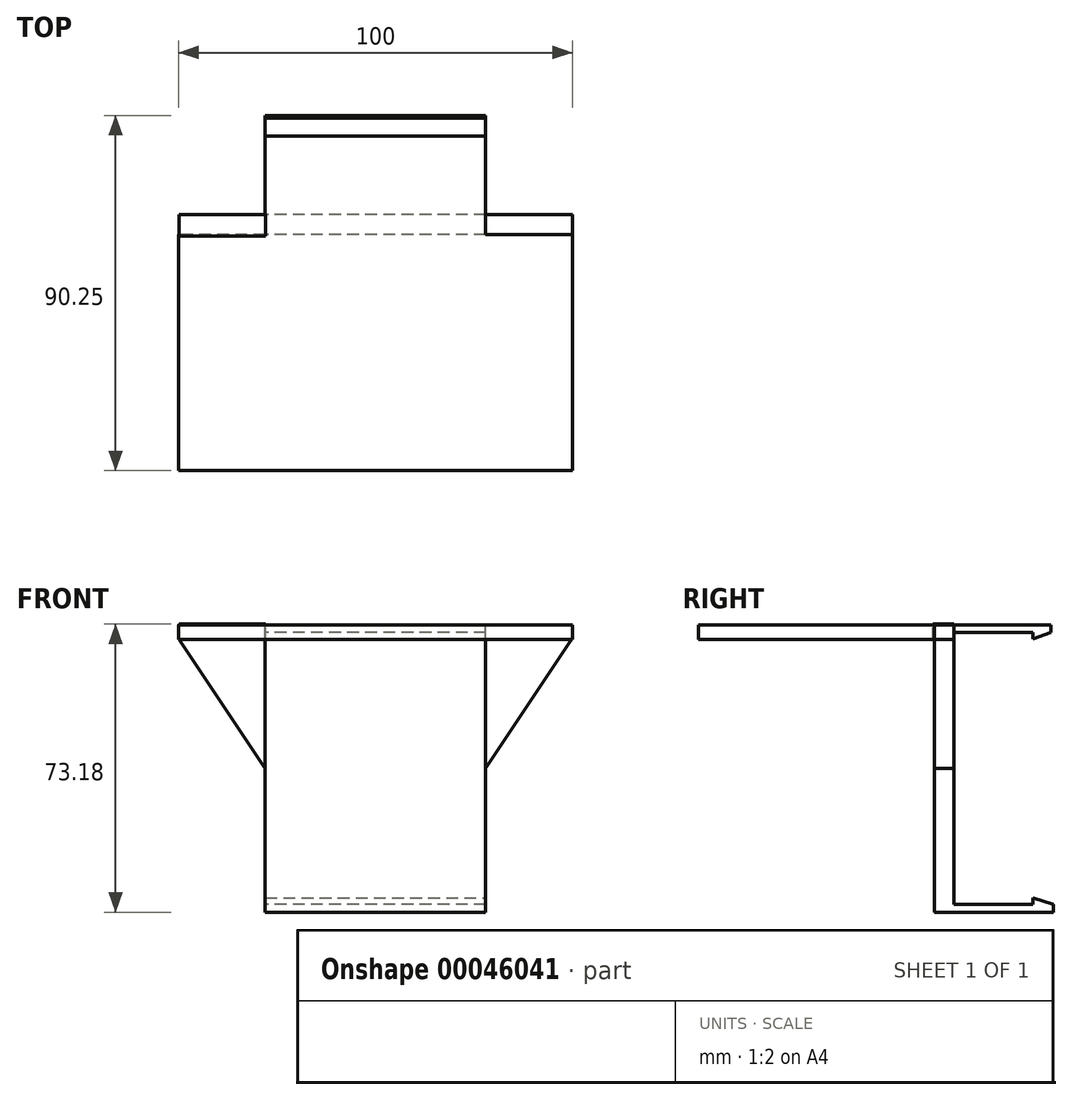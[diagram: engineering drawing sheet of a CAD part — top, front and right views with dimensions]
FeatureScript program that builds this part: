
annotation { "Feature Type Name" : "Feature", "Feature Type Description" : "" }
export const myFeature = defineFeature(function(context is Context, id is Id, definition is map)
    precondition{}
    {
        {
            var Q0;
            Q0=qCreatedBy(makeId("Front.planeOp"),FACE);
            var sketch = newSketch(context, id + "F0", { "sketchPlane" : qUnion([Q0])});
            skLineSegment(sketch, "E0.rect.bottom", {"start": v(28, -34.5) * mm, "end": v(-28, -34.5) * mm});
            skLineSegment(sketch, "E0.rect.top", {"start": v(28, 34.5) * mm, "end": v(-28, 34.5) * mm});
            skLineSegment(sketch, "E0.rect.left", {"start": v(28, -34.5) * mm, "end": v(28, 34.5) * mm});
            skLineSegment(sketch, "E0.rect.right", {"start": v(-28, -34.5) * mm, "end": v(-28, 34.5) * mm});
            skPoint(sketch, "E0.rect.middle", {"position": v(0, 0) * mm});
            skSolve(sketch);
        }
        {
            var Q0;
            Q0=makeQuery(id+"F0.imprint","IMPRINT",FACE,{"disambiguationData":[TD([[makeQuery(id+"F0.imprint","IMPRINT",EDGE,{"derivedFrom":sQuery(id+"F0.wireOp",EDGE,"E0.rect.bottom")}),-1.0]])]});
            extrude(context, id + "F1", {"entities" : qUnion([Q0]), "depth" : 5 * mm});
        }
        {
            var Q0;
            Q0=makeQuery(id+"F1.opExtrude","SWEPT_FACE",FACE,{"disambiguationData":[OSD([sQuery(id+"F0.wireOp",EDGE,"E0.rect.top")])]});
            var sketch = newSketch(context, id + "F2", { "sketchPlane" : qUnion([Q0])});
            skPoint(sketch, "E1.oppositeSnap0", {"position": v(28, -2.5) * mm});
            skLineSegment(sketch, "E1.bottom", {"start": v(-28, -5) * mm, "end": v(28, -5) * mm});
            skLineSegment(sketch, "E1.top", {"start": v(-28, 20) * mm, "end": v(28, 20) * mm});
            skLineSegment(sketch, "E1.left", {"start": v(-28, -5) * mm, "end": v(-28, 20) * mm});
            skLineSegment(sketch, "E1.right", {"start": v(28, -5) * mm, "end": v(28, 20) * mm});
            skSolve(sketch);
        }
        {
            var Q0;
            {var subQ2=sQuery(id+"F2.wireOp",EDGE,"E1.top");Q0=makeQuery(id+"F2.imprint","IMPRINT",FACE,{"disambiguationData":[TD([[makeQuery(id+"F2.imprint","IMPRINT",EDGE,{"derivedFrom":subQ2}),-1.0]])]});}
            var Q1;
            {var subQ2=sQuery(id+"F2.wireOp",EDGE,"E1.bottom");Q1=makeQuery(id+"F2.imprint","IMPRINT",FACE,{"disambiguationData":[TD([[makeQuery(id+"F2.imprint","IMPRINT",EDGE,{"derivedFrom":subQ2}),-1.0]])]});}
            extrude(context, id + "F3", {"entities" : qUnion([Q0, Q1]), "operationType" : NewBodyOperationType.ADD, "depth" : 2 * mm});
        }
        {
            var Q0;
            Q0=makeQuery(id+"F3.boolean.opBoolean","MERGE",FACE,{"derivedFrom":[makeQuery(id+"F1.opExtrude","SWEPT_FACE",FACE,{"disambiguationData":[OSD([sQuery(id+"F0.wireOp",EDGE,"E0.rect.right")])]}),makeQuery(id+"F3.opExtrude","SWEPT_FACE",FACE,{"disambiguationData":[OSD([sQuery(id+"F2.wireOp",EDGE,"E1.left")])]})]});
            var sketch = newSketch(context, id + "F4", { "sketchPlane" : qUnion([Q0])});
            skLineSegment(sketch, "E2.bottom", {"start": v(-20, 34.5) * mm, "end": v(-24.6, 34.5) * mm});
            skLineSegment(sketch, "E2.top", {"start": v(-20, 36.44) * mm, "end": v(-24.6, 36.44) * mm});
            skLineSegment(sketch, "E2.left", {"start": v(-20, 34.5) * mm, "end": v(-20, 36.44) * mm});
            skLineSegment(sketch, "E2.right", {"start": v(-24.6, 34.5) * mm, "end": v(-24.6, 36.44) * mm});
            skLineSegment(sketch, "E3", {"start": v(-24.6, 34.5) * mm, "end": v(-20, 32.91) * mm});
            skLineSegment(sketch, "E4", {"start": v(-20, 32.91) * mm, "end": v(-20, 34.5) * mm});
            skSolve(sketch);
        }
        {
            var Q0;
            Q0=makeQuery(id+"F4.imprint","IMPRINT",FACE,{"disambiguationData":[TD([[makeQuery(id+"F4.imprint","IMPRINT",EDGE,{"derivedFrom":sQuery(id+"F4.wireOp",EDGE,"E2.bottom")}),1.0]])]});
            var Q1;
            Q1=makeQuery(id+"F4.imprint","IMPRINT",FACE,{"disambiguationData":[TD([[makeQuery(id+"F4.imprint","IMPRINT",EDGE,{"derivedFrom":sQuery(id+"F4.wireOp",EDGE,"E2.bottom")}),-1.0]])]});
            extrude(context, id + "F5", {"entities" : qUnion([Q0, Q1]), "operationType" : NewBodyOperationType.ADD, "oppositeDirection" : true, "depth" : 56 * mm});
        }
        {
            var Q0;
            Q0=makeQuery(id+"F1.opExtrude","SWEPT_FACE",FACE,{"disambiguationData":[OSD([sQuery(id+"F0.wireOp",EDGE,"E0.rect.bottom")])]});
            var sketch = newSketch(context, id + "F6", { "sketchPlane" : qUnion([Q0])});
            skPoint(sketch, "E5.oppositeSnap0", {"position": v(-28, 2.5) * mm});
            skLineSegment(sketch, "E5.bottom", {"start": v(28, 5) * mm, "end": v(-28, 5) * mm});
            skLineSegment(sketch, "E5.top", {"start": v(28, -20) * mm, "end": v(-28, -20) * mm});
            skLineSegment(sketch, "E5.left", {"start": v(28, 5) * mm, "end": v(28, -20) * mm});
            skLineSegment(sketch, "E5.right", {"start": v(-28, 5) * mm, "end": v(-28, -20) * mm});
            skSolve(sketch);
        }
        {
            var Q0;
            {var subQ1=sQuery(id+"F6.wireOp",EDGE,"E5.top");Q0=makeQuery(id+"F6.imprint","IMPRINT",FACE,{"disambiguationData":[TD([[makeQuery(id+"F6.imprint","IMPRINT",EDGE,{"derivedFrom":subQ1}),-1.0]])]});}
            var Q1;
            {var subQ2=sQuery(id+"F6.wireOp",EDGE,"E5.bottom");Q1=makeQuery(id+"F6.imprint","IMPRINT",FACE,{"disambiguationData":[TD([[makeQuery(id+"F6.imprint","IMPRINT",EDGE,{"derivedFrom":subQ2}),1.0]])]});}
            extrude(context, id + "F7", {"entities" : qUnion([Q0, Q1]), "operationType" : NewBodyOperationType.ADD, "depth" : 2 * mm});
        }
        {
            var Q0;
            Q0=makeQuery(id+"F7.boolean.opBoolean","MERGE",FACE,{"derivedFrom":[makeQuery(id+"F5.boolean.opBoolean","MERGE",FACE,{"derivedFrom":[makeQuery(id+"F3.boolean.opBoolean","MERGE",FACE,{"derivedFrom":[makeQuery(id+"F1.opExtrude","SWEPT_FACE",FACE,{"disambiguationData":[OSD([sQuery(id+"F0.wireOp",EDGE,"E0.rect.left")])]}),makeQuery(id+"F3.opExtrude","SWEPT_FACE",FACE,{"disambiguationData":[OSD([sQuery(id+"F2.wireOp",EDGE,"E1.right")])]})]}),makeQuery(id+"F5.opExtrude","CAP_FACE",FACE,{"disambiguationData":[OSD([sQuery(id+"F4.wireOp",EDGE,"E2.top"),sQuery(id+"F4.wireOp",EDGE,"E2.left"),sQuery(id+"F4.wireOp",EDGE,"E2.right"),sQuery(id+"F4.wireOp",EDGE,"E3"),sQuery(id+"F4.wireOp",EDGE,"E4")])],"isStart":false})]}),makeQuery(id+"F7.opExtrude","SWEPT_FACE",FACE,{"disambiguationData":[OSD([sQuery(id+"F6.wireOp",EDGE,"E5.left")])]})]});
            var sketch = newSketch(context, id + "F8", { "sketchPlane" : qUnion([Q0])});
            skLineSegment(sketch, "E6.bottom", {"start": v(20, -34.5) * mm, "end": v(25.25, -34.5) * mm});
            skLineSegment(sketch, "E6.top", {"start": v(20, -36.5) * mm, "end": v(25.25, -36.5) * mm});
            skLineSegment(sketch, "E6.left", {"start": v(20, -34.5) * mm, "end": v(20, -36.5) * mm});
            skLineSegment(sketch, "E6.right", {"start": v(25.25, -34.5) * mm, "end": v(25.25, -36.5) * mm});
            skLineSegment(sketch, "E7", {"start": v(25.25, -34.5) * mm, "end": v(20, -32.85) * mm});
            skLineSegment(sketch, "E8", {"start": v(20, -32.85) * mm, "end": v(20, -34.5) * mm});
            skSolve(sketch);
        }
        {
            var Q0;
            Q0=makeQuery(id+"F8.imprint","IMPRINT",FACE,{"disambiguationData":[TD([[makeQuery(id+"F8.imprint","IMPRINT",EDGE,{"derivedFrom":sQuery(id+"F8.wireOp",EDGE,"E6.bottom")}),1.0]])]});
            var Q1;
            Q1=makeQuery(id+"F8.imprint","IMPRINT",FACE,{"disambiguationData":[TD([[makeQuery(id+"F8.imprint","IMPRINT",EDGE,{"derivedFrom":sQuery(id+"F8.wireOp",EDGE,"E6.bottom")}),-1.0]])]});
            var Q2;
            Q2=sQuery(id+"F8.wireOp",EDGE,"E6.right");
            extrude(context, id + "F9", {"entities" : qUnion([Q0, Q1]), "operationType" : NewBodyOperationType.ADD, "surfaceEntities" : qUnion([Q2]), "oppositeDirection" : true, "depth" : 56 * mm});
        }
        {
            var Q0;
            Q0=makeQuery(id+"F7.boolean.opBoolean","MERGE",FACE,{"derivedFrom":[makeQuery(id+"F3.boolean.opBoolean","MERGE",FACE,{"derivedFrom":[makeQuery(id+"F1.opExtrude","CAP_FACE",FACE,{"disambiguationData":[OSD([sQuery(id+"F0.wireOp",EDGE,"E0.rect.bottom"),sQuery(id+"F0.wireOp",EDGE,"E0.rect.top"),sQuery(id+"F0.wireOp",EDGE,"E0.rect.left"),sQuery(id+"F0.wireOp",EDGE,"E0.rect.right")])],"isStart":false}),makeQuery(id+"F3.opExtrude","SWEPT_FACE",FACE,{"disambiguationData":[OSD([sQuery(id+"F2.wireOp",EDGE,"E1.bottom")])]})]}),makeQuery(id+"F7.opExtrude","SWEPT_FACE",FACE,{"disambiguationData":[OSD([sQuery(id+"F6.wireOp",EDGE,"E5.bottom")])]})]});
            var sketch = newSketch(context, id + "F10", { "sketchPlane" : qUnion([Q0])});
            skLineSegment(sketch, "E9.bottom", {"start": v(50, 36.5) * mm, "end": v(-50, 36.5) * mm});
            skLineSegment(sketch, "E9.top", {"start": v(50, 32.78) * mm, "end": v(-50, 32.78) * mm});
            skLineSegment(sketch, "E9.left", {"start": v(50, 36.5) * mm, "end": v(50, 32.78) * mm});
            skLineSegment(sketch, "E9.right", {"start": v(-50, 36.5) * mm, "end": v(-50, 32.78) * mm});
            skSolve(sketch);
        }
        {
            var Q0;
            {var subQ3=sQuery(id+"F10.wireOp",EDGE,"E9.left");Q0=makeQuery(id+"F10.imprint","IMPRINT",FACE,{"disambiguationData":[TD([[makeQuery(id+"F10.imprint","IMPRINT",EDGE,{"derivedFrom":subQ3}),-1.0]])]});}
            var Q1;
            {var subQ0=sQuery(id+"F2.wireOp",EDGE,"E1.bottom");var subQ1=sQuery(id+"F6.wireOp",EDGE,"E5.bottom");var subQ5=sQuery(id+"F10.wireOp",EDGE,"E9.bottom");var subQ7=makeQuery(id+"F7.boolean.opBoolean","MERGE",EDGE,{"derivedFrom":[makeQuery(id+"F3.boolean.opBoolean","MERGE",EDGE,{"derivedFrom":[makeQuery(id+"F1.opExtrude","CAP_EDGE",EDGE,{"disambiguationData":[OSD([sQuery(id+"F0.wireOp",EDGE,"E0.rect.left")])],"isStart":false}),makeQuery(id+"F3.opExtrude","SWEPT_EDGE",EDGE,{"disambiguationData":[OSD([subQ0,sQuery(id+"F2.wireOp",EDGE,"E1.right")])]})]}),makeQuery(id+"F7.opExtrude","SWEPT_EDGE",EDGE,{"disambiguationData":[OSD([subQ1,sQuery(id+"F6.wireOp",EDGE,"E5.left")])]})]});var subQ9=makeQuery(id+"F10.imprint","INTERSECT",VERTEX,{"derivedFrom":[subQ7,subQ5]});Q1=makeQuery(id+"F10.imprint","IMPRINT",FACE,{"disambiguationData":[TD([[makeQuery(id+"F10.imprint","IMPRINT",EDGE,{"disambiguationData":[TD([[subQ9,-1.0]])],"derivedFrom":subQ5}),1.0]])]});}
            var Q2;
            {var subQ0=sQuery(id+"F10.wireOp",EDGE,"E9.right");Q2=makeQuery(id+"F10.imprint","IMPRINT",FACE,{"disambiguationData":[TD([[makeQuery(id+"F10.imprint","IMPRINT",EDGE,{"derivedFrom":subQ0}),1.0]])]});}
            extrude(context, id + "F11", {"entities" : qUnion([Q0, Q1, Q2]), "operationType" : NewBodyOperationType.ADD, "depth" : 60 * mm});
        }
        {
            var Q0;
            Q0=makeQuery(id+"F7.boolean.opBoolean","MERGE",FACE,{"derivedFrom":[makeQuery(id+"F3.boolean.opBoolean","MERGE",FACE,{"derivedFrom":[makeQuery(id+"F1.opExtrude","CAP_FACE",FACE,{"disambiguationData":[OSD([sQuery(id+"F0.wireOp",EDGE,"E0.rect.bottom"),sQuery(id+"F0.wireOp",EDGE,"E0.rect.top"),sQuery(id+"F0.wireOp",EDGE,"E0.rect.left"),sQuery(id+"F0.wireOp",EDGE,"E0.rect.right")])],"isStart":false}),makeQuery(id+"F3.opExtrude","SWEPT_FACE",FACE,{"disambiguationData":[OSD([sQuery(id+"F2.wireOp",EDGE,"E1.bottom")])]})]}),makeQuery(id+"F7.opExtrude","SWEPT_FACE",FACE,{"disambiguationData":[OSD([sQuery(id+"F6.wireOp",EDGE,"E5.bottom")])]})]});
            var sketch = newSketch(context, id + "F12", { "sketchPlane" : qUnion([Q0])});
            skLineSegment(sketch, "E10", {"start": v(-28, 32.78) * mm, "end": v(-49.95, 32.78) * mm});
            skLineSegment(sketch, "E11", {"start": v(-49.95, 32.78) * mm, "end": v(-28, 0) * mm});
            skLineSegment(sketch, "E12", {"start": v(28, 32.78) * mm, "end": v(49.84, 32.78) * mm});
            skLineSegment(sketch, "E13", {"start": v(49.84, 32.78) * mm, "end": v(28, 0) * mm});
            skPoint(sketch, "E14", {"position": v(-28, -1.86) * mm});
            skSolve(sketch);
        }
        {
            var Q0;
            {var subQ30=sQuery(id+"F12.wireOp",EDGE,"E12");Q0=makeQuery(id+"F12.imprint","IMPRINT",FACE,{"disambiguationData":[TD([[makeQuery(id+"F12.imprint","IMPRINT",EDGE,{"derivedFrom":subQ30}),-1.0]])]});}
            var Q1;
            {var subQ30=sQuery(id+"F12.wireOp",EDGE,"E10");Q1=makeQuery(id+"F12.imprint","IMPRINT",FACE,{"disambiguationData":[TD([[makeQuery(id+"F12.imprint","IMPRINT",EDGE,{"derivedFrom":subQ30}),1.0]])]});}
            extrude(context, id + "F13", {"entities" : qUnion([Q0, Q1]), "oppositeDirection" : true, "depth" : 5 * mm});
        }
        {
            var Q0;
            Q0=makeQuery(id+"F13.opExtrude","CAP_FACE",FACE,{"disambiguationData":[OSD([sQuery(id+"F0.wireOp",EDGE,"E0.rect.right"),sQuery(id+"F2.wireOp",EDGE,"E1.bottom"),sQuery(id+"F2.wireOp",EDGE,"E1.left"),sQuery(id+"F6.wireOp",EDGE,"E5.bottom"),sQuery(id+"F6.wireOp",EDGE,"E5.right"),sQuery(id+"F12.wireOp",EDGE,"E10"),sQuery(id+"F12.wireOp",EDGE,"E11")])],"isStart":false});
            var sketch = newSketch(context, id + "F14", { "sketchPlane" : qUnion([Q0])});
            skLineSegment(sketch, "E15.bottom", {"start": v(49.95, 32.78) * mm, "end": v(27.95, 32.78) * mm});
            skLineSegment(sketch, "E15.top", {"start": v(49.95, 36.68) * mm, "end": v(27.95, 36.68) * mm});
            skLineSegment(sketch, "E15.left", {"start": v(49.95, 32.78) * mm, "end": v(49.95, 36.68) * mm});
            skLineSegment(sketch, "E15.right", {"start": v(27.95, 32.78) * mm, "end": v(27.95, 36.68) * mm});
            skSolve(sketch);
        }
        {
            var Q0;
            Q0=makeQuery(id+"F14.imprint","IMPRINT",FACE,{"disambiguationData":[TD([[makeQuery(id+"F14.imprint","IMPRINT",EDGE,{"derivedFrom":sQuery(id+"F14.wireOp",EDGE,"E15.bottom")}),1.0]])]});
            extrude(context, id + "F15", {"entities" : qUnion([Q0]), "oppositeDirection" : true, "depth" : 5.45 * mm});
        }
        {
            var Q0;
            {var subQ0=sQuery(id+"F10.wireOp",EDGE,"E9.bottom");var subQ1=sQuery(id+"F10.wireOp",EDGE,"E9.top");var subQ2=sQuery(id+"F10.wireOp",EDGE,"E9.left");var subQ5=sQuery(id+"F0.wireOp",EDGE,"E0.rect.left");Q0=makeQuery(id+"F11.boolean.opBoolean","SPLIT",FACE,{"disambiguationData":[TD([makeQuery(id+"F1.opExtrude","SWEPT_FACE",FACE,{"disambiguationData":[OSD([subQ5])]})])],"derivedFrom":makeQuery(id+"F11.opExtrude","CAP_FACE",FACE,{"disambiguationData":[OSD([subQ0,subQ1,subQ2,sQuery(id+"F10.wireOp",EDGE,"E9.right")])],"isStart":true})});}
            var sketch = newSketch(context, id + "F16", { "sketchPlane" : qUnion([Q0])});
            skLineSegment(sketch, "E16.bottom", {"start": v(-50, 32.78) * mm, "end": v(-28, 32.78) * mm});
            skLineSegment(sketch, "E16.top", {"start": v(-50, 36.5) * mm, "end": v(-28, 36.5) * mm});
            skLineSegment(sketch, "E16.left", {"start": v(-50, 32.78) * mm, "end": v(-50, 36.5) * mm});
            skLineSegment(sketch, "E16.right", {"start": v(-28, 32.78) * mm, "end": v(-28, 36.5) * mm});
            skSolve(sketch);
        }
        {
            var Q0;
            Q0=makeQuery(id+"F16.imprint","IMPRINT",FACE,{"disambiguationData":[TD([[makeQuery(id+"F16.imprint","IMPRINT",EDGE,{"derivedFrom":sQuery(id+"F16.wireOp",EDGE,"E16.bottom")}),1.0]])]});
            extrude(context, id + "F17", {"entities" : qUnion([Q0]), "depth" : 5 * mm});
        }
    });
